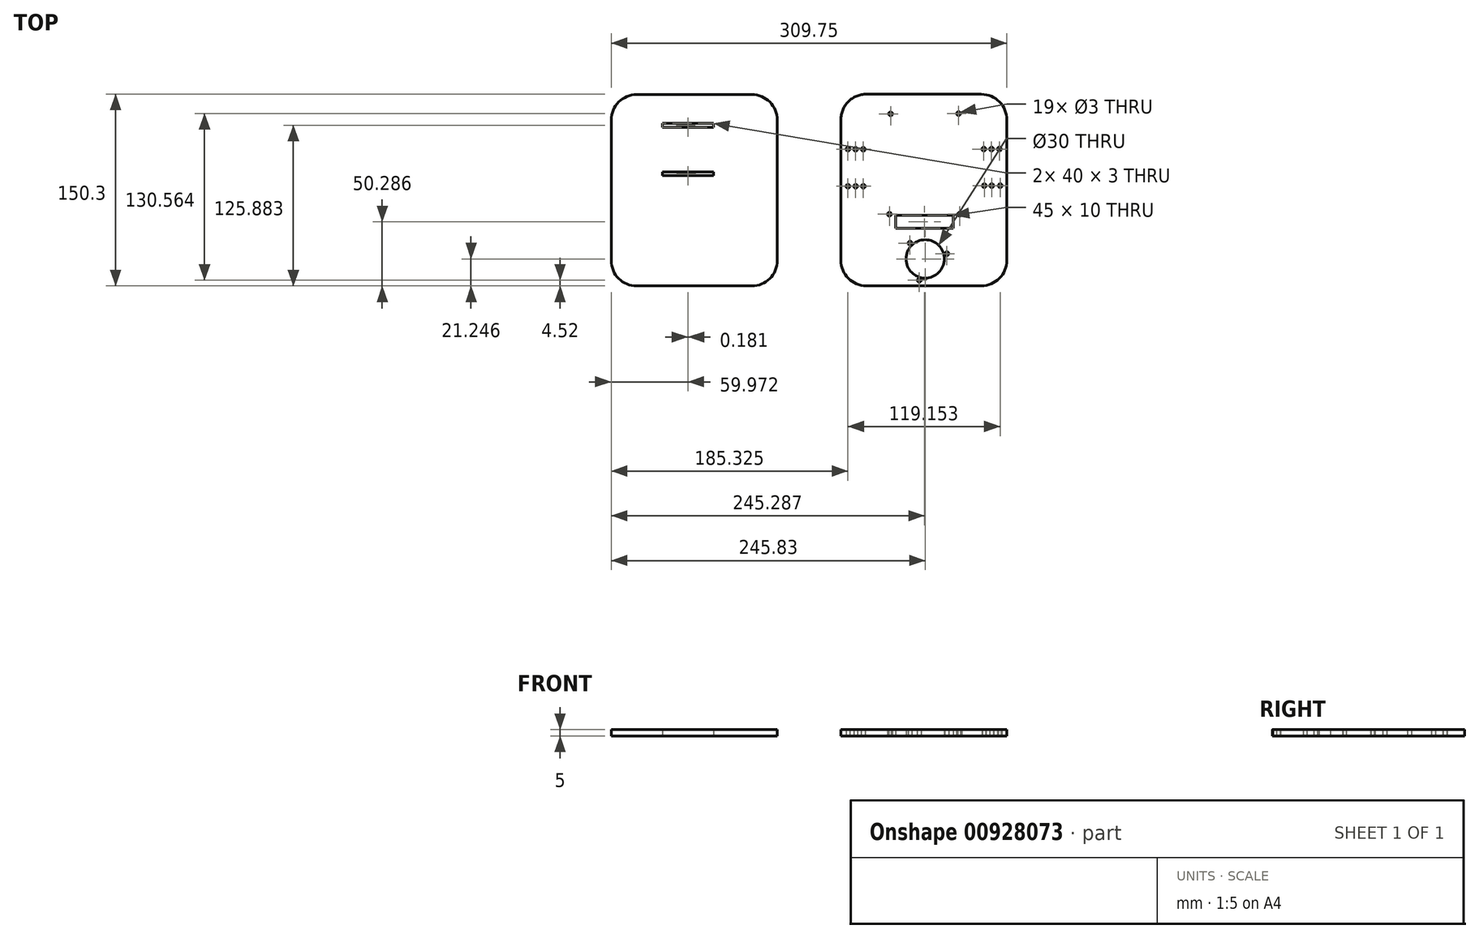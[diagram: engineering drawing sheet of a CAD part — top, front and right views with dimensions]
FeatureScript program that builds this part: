
annotation { "Feature Type Name" : "Feature", "Feature Type Description" : "" }
export const myFeature = defineFeature(function(context is Context, id is Id, definition is map)
    precondition{}
    {
        {
            var Q0;
            Q0=qCreatedBy(makeId("Top.planeOp"),FACE);
            var sketch = newSketch(context, id + "F0", { "sketchPlane" : qUnion([Q0])});
            skCircle(sketch, "E0", {"center": v(4.82, -47.75) * mm, "radius": 1.5 * mm});
            skCircle(sketch, "E1", {"center": v(4.82, -76.84) * mm, "radius": 1.5 * mm});
            skCircle(sketch, "E2", {"center": v(16.82, -76.86) * mm, "radius": 1.5 * mm});
            skCircle(sketch, "E3", {"center": v(10.82, -47.85) * mm, "radius": 1.5 * mm});
            skCircle(sketch, "E4", {"center": v(16.82, -47.86) * mm, "radius": 1.5 * mm});
            skCircle(sketch, "E5", {"center": v(10.82, -76.85) * mm, "radius": 1.5 * mm});
            skCircle(sketch, "E6.MirrorC", {"center": v(60.65, -150.5) * mm, "radius": 1.5 * mm});
            skCircle(sketch, "E7.MirrorC", {"center": v(65.33, -133.77) * mm, "radius": 15 * mm});
            skCircle(sketch, "E8.MirrorC", {"center": v(82.23, -129.66) * mm, "radius": 1.5 * mm});
            skCircle(sketch, "E9.MirrorC", {"center": v(53.4, -121.4) * mm, "radius": 1.5 * mm});
            skCircle(sketch, "E10.MirrorC", {"center": v(65.33, -133.77) * mm, "radius": 19 * mm, "construction": true});
            skCircle(sketch, "E11.MirrorC", {"center": v(111.56, -76.4) * mm, "radius": 1.5 * mm});
            skCircle(sketch, "E12.MirrorC", {"center": v(111.22, -47.75) * mm, "radius": 1.5 * mm});
            skCircle(sketch, "E13.MirrorC", {"center": v(117.38, -76.39) * mm, "radius": 1.5 * mm});
            skCircle(sketch, "E14.MirrorC", {"center": v(117.24, -47.75) * mm, "radius": 1.5 * mm});
            skCircle(sketch, "E15.MirrorC", {"center": v(123.98, -76.4) * mm, "radius": 1.5 * mm});
            skCircle(sketch, "E16.MirrorC", {"center": v(123.35, -47.75) * mm, "radius": 1.5 * mm});
            skLineSegment(sketch, "E17", {"start": v(31.23, -5.15) * mm, "end": v(31.23, -26.15) * mm});
            skLineSegment(sketch, "E18", {"start": v(31.23, -26.15) * mm, "end": v(45.23, -26.15) * mm});
            skLineSegment(sketch, "E19", {"start": v(45.23, -26.15) * mm, "end": v(45.23, -5.15) * mm});
            skCircle(sketch, "E20", {"center": v(38.23, -20.15) * mm, "radius": 1.5 * mm});
            skPoint(sketch, "E21.endSnap0", {"position": v(38.23, -26.15) * mm});
            skCircle(sketch, "E22.MirrorC", {"center": v(91.44, -19.94) * mm, "radius": 1.5 * mm});
            skLineSegment(sketch, "E23.MirrorCS", {"start": v(98.4, -25.97) * mm, "end": v(84.4, -25.9) * mm});
            skLineSegment(sketch, "E24.MirrorCS", {"start": v(98.52, -4.97) * mm, "end": v(98.4, -25.97) * mm});
            skPoint(sketch, "E25.MirrorP", {"position": v(91.4, -25.94) * mm});
            skLineSegment(sketch, "E26.MirrorCS", {"start": v(84.4, -25.9) * mm, "end": v(84.52, -4.9) * mm});
            skLineSegment(sketch, "E27.bottom", {"start": v(19.28, -4.72) * mm, "end": v(109.28, -4.83) * mm});
            skLineSegment(sketch, "E27.left", {"start": v(-0.75, -24.72) * mm, "end": v(-0.75, -134.85) * mm});
            skLineSegment(sketch, "E27.right", {"start": v(129.25, -24.83) * mm, "end": v(129.25, -134.85) * mm});
            skLineSegment(sketch, "E28", {"start": v(19.25, -154.85) * mm, "end": v(109.25, -154.85) * mm});
            skPoint(sketch, "E29.orphan", {"position": v(129.25, -212.76) * mm});
            skPoint(sketch, "E30.orphan", {"position": v(-0.75, -212.6) * mm});
            skLineSegment(sketch, "E31.bottom", {"start": v(96.29, -112.73) * mm, "end": v(33.29, -112.73) * mm});
            skLineSegment(sketch, "E31.top", {"start": v(96.29, -84.73) * mm, "end": v(33.29, -84.73) * mm});
            skLineSegment(sketch, "E31.left", {"start": v(96.29, -112.73) * mm, "end": v(96.29, -84.73) * mm});
            skLineSegment(sketch, "E31.right", {"start": v(33.29, -112.73) * mm, "end": v(33.29, -84.73) * mm});
            skCircle(sketch, "E32", {"center": v(37.29, -98.73) * mm, "radius": 1.5 * mm});
            skCircle(sketch, "E33.MirrorC", {"center": v(92.29, -98.73) * mm, "radius": 1.5 * mm});
            skLineSegment(sketch, "E34.bottom", {"start": v(42.29, -99.73) * mm, "end": v(87.29, -99.73) * mm});
            skLineSegment(sketch, "E34.top", {"start": v(42.29, -109.73) * mm, "end": v(87.29, -109.73) * mm});
            skLineSegment(sketch, "E34.left", {"start": v(42.29, -99.73) * mm, "end": v(42.29, -109.73) * mm});
            skLineSegment(sketch, "E34.right", {"start": v(87.29, -99.73) * mm, "end": v(87.29, -109.73) * mm});
            skPoint(sketch, "E35.middle", {"position": v(64.79, -98.73) * mm});
            skPoint(sketch, "E36.visualSharp", {"position": v(129.25, -154.85) * mm});
            skArc(sketch, "E36.filletArc", {"start": v(109.25, -154.85) * mm, "mid": v(123.4, -149) * mm, "end": v(129.25, -134.85) * mm});
            skPoint(sketch, "E37.visualSharp", {"position": v(-0.75, -154.85) * mm});
            skArc(sketch, "E37.filletArc", {"start": v(-0.75, -134.85) * mm, "mid": v(5.11, -149) * mm, "end": v(19.25, -154.85) * mm});
            skPoint(sketch, "E38.visualSharp", {"position": v(129.25, -4.85) * mm});
            skArc(sketch, "E38.filletArc", {"start": v(129.25, -24.83) * mm, "mid": v(123.4, -10.7) * mm, "end": v(109.28, -4.83) * mm});
            skPoint(sketch, "E39.visualSharp", {"position": v(-0.75, -4.7) * mm});
            skArc(sketch, "E39.filletArc", {"start": v(19.28, -4.72) * mm, "mid": v(5.12, -10.57) * mm, "end": v(-0.75, -24.72) * mm});
            skLineSegment(sketch, "E40.bottom", {"start": v(-160.5, -5.02) * mm, "end": v(-70.5, -5.02) * mm});
            skLineSegment(sketch, "E40.top", {"start": v(-160.5, -155.02) * mm, "end": v(-70.5, -155.02) * mm});
            skLineSegment(sketch, "E40.left", {"start": v(-180.5, -25.02) * mm, "end": v(-180.5, -135.02) * mm});
            skLineSegment(sketch, "E40.right", {"start": v(-50.5, -25.02) * mm, "end": v(-50.5, -135.02) * mm});
            skPoint(sketch, "E41.visualSharp", {"position": v(-50.5, -5.02) * mm});
            skArc(sketch, "E41.filletArc", {"start": v(-50.5, -25.02) * mm, "mid": v(-56.35, -10.88) * mm, "end": v(-70.5, -5.02) * mm});
            skPoint(sketch, "E42.visualSharp", {"position": v(-180.5, -5.02) * mm});
            skArc(sketch, "E42.filletArc", {"start": v(-160.5, -5.02) * mm, "mid": v(-174.64, -10.88) * mm, "end": v(-180.5, -25.02) * mm});
            skPoint(sketch, "E43.visualSharp", {"position": v(-180.5, -155.02) * mm});
            skArc(sketch, "E43.filletArc", {"start": v(-180.5, -135.02) * mm, "mid": v(-174.64, -149.17) * mm, "end": v(-160.5, -155.02) * mm});
            skPoint(sketch, "E44.visualSharp", {"position": v(-50.5, -155.02) * mm});
            skArc(sketch, "E44.filletArc", {"start": v(-70.5, -155.02) * mm, "mid": v(-56.35, -149.17) * mm, "end": v(-50.5, -135.02) * mm});
            skPoint(sketch, "E45.middle", {"position": v(-120.35, -67.14) * mm});
            skLineSegment(sketch, "E46.bottom", {"start": v(-100.35, -68.64) * mm, "end": v(-140.35, -68.64) * mm});
            skLineSegment(sketch, "E46.top", {"start": v(-100.35, -65.64) * mm, "end": v(-140.35, -65.64) * mm});
            skLineSegment(sketch, "E46.left", {"start": v(-100.35, -68.64) * mm, "end": v(-100.35, -65.64) * mm});
            skLineSegment(sketch, "E46.right", {"start": v(-140.35, -68.64) * mm, "end": v(-140.35, -65.64) * mm});
            skLineSegment(sketch, "E47.bottom", {"start": v(-100.53, -30.64) * mm, "end": v(-140.53, -30.64) * mm});
            skLineSegment(sketch, "E47.top", {"start": v(-100.53, -27.64) * mm, "end": v(-140.53, -27.64) * mm});
            skLineSegment(sketch, "E47.left", {"start": v(-100.53, -30.64) * mm, "end": v(-100.53, -27.64) * mm});
            skLineSegment(sketch, "E47.right", {"start": v(-140.53, -30.64) * mm, "end": v(-140.53, -27.64) * mm});
            skSolve(sketch);
        }
        {
            var Q0;
            Q0=makeQuery(id+"F0.imprint","IMPRINT",FACE,{"disambiguationData":[TD([[makeQuery(id+"F0.imprint","IMPRINT",EDGE,{"derivedFrom":sQuery(id+"F0.wireOp",EDGE,"E0")}),-1.0]])]});
            var Q1;
            {var subQ1=sQuery(id+"F0.wireOp",EDGE,"E17");Q1=makeQuery(id+"F0.imprint","IMPRINT",FACE,{"disambiguationData":[TD([[makeQuery(id+"F0.imprint","IMPRINT",EDGE,{"derivedFrom":subQ1}),1.0]])]});}
            var Q2;
            Q2=makeQuery(id+"F0.imprint","IMPRINT",FACE,{"disambiguationData":[TD([[makeQuery(id+"F0.imprint","IMPRINT",EDGE,{"derivedFrom":sQuery(id+"F0.wireOp",EDGE,"7aQJlTwi-yZK0-z67h-T5hG-59ZMhR0VvL68.bottom")}),-1.0]])]});
            var Q3;
            Q3=makeQuery(id+"F0.imprint","IMPRINT",FACE,{"disambiguationData":[TD([[makeQuery(id+"F0.imprint","IMPRINT",EDGE,{"derivedFrom":sQuery(id+"F0.wireOp",EDGE,"E31.bottom")}),-1.0]])]});
            extrude(context, id + "F1", {"entities" : qUnion([Q0, Q1, Q2, Q3]), "depth" : 5 * mm, "offsetDistance" : 25 * mm});
        }
        {
            var Q0;
            Q0=makeQuery(id+"F0.imprint","IMPRINT",FACE,{"disambiguationData":[TD([[makeQuery(id+"F0.imprint","IMPRINT",EDGE,{"derivedFrom":sQuery(id+"F0.wireOp",EDGE,"E40.bottom")}),-1.0]])]});
            extrude(context, id + "F2", {"entities" : qUnion([Q0]), "depth" : 5 * mm, "offsetDistance" : 25 * mm});
        }
    });
